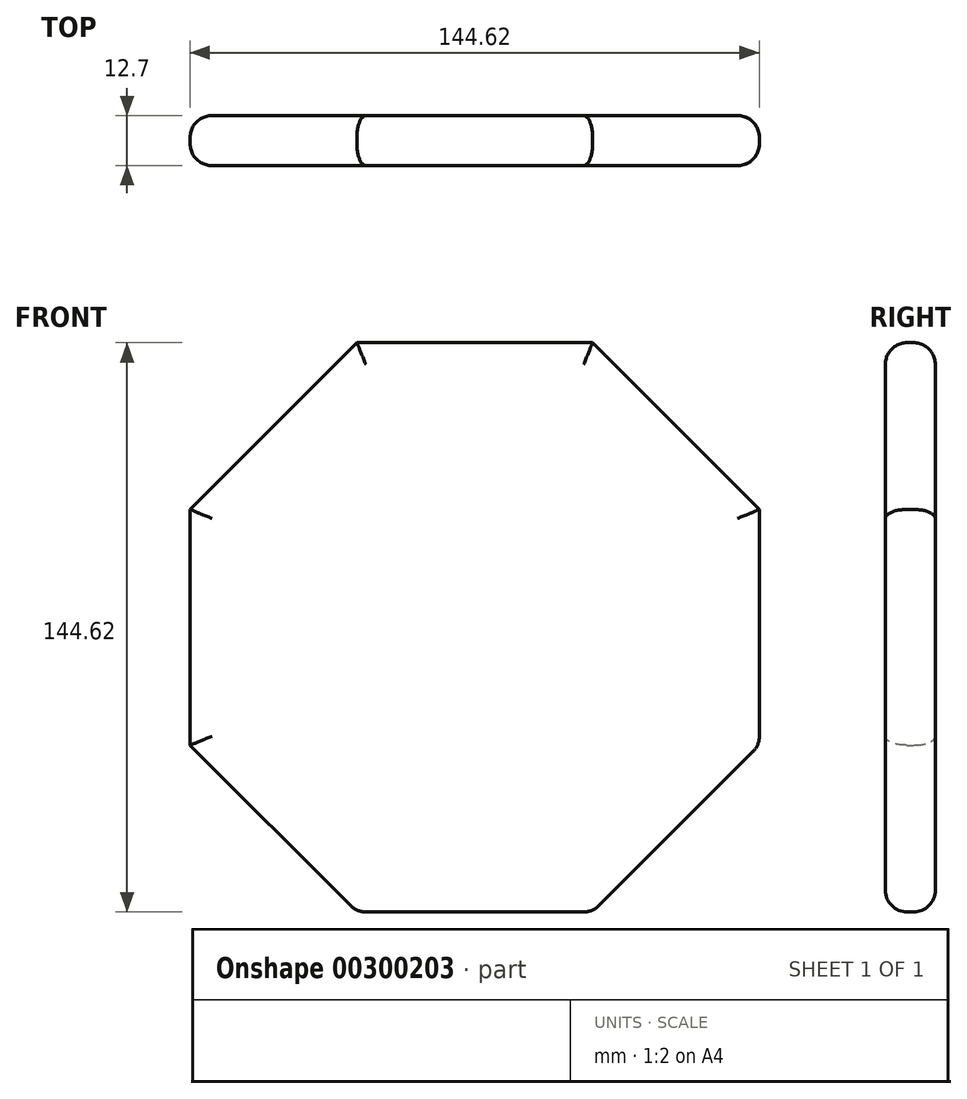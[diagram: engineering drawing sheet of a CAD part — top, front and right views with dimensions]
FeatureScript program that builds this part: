
annotation { "Feature Type Name" : "Feature", "Feature Type Description" : "" }
export const myFeature = defineFeature(function(context is Context, id is Id, definition is map)
    precondition{}
    {
        {
            var Q0;
            Q0=qCreatedBy(makeId("Front.planeOp"),FACE);
            var sketch = newSketch(context, id + "F0", { "sketchPlane" : qUnion([Q0])});
            skCircle(sketch, "E0.cCircle", {"center": v(0, 0) * mm, "radius": 72.31 * mm, "construction": true});
            skLineSegment(sketch, "E0.0", {"start": v(-72.31, -29.95) * mm, "end": v(-72.31, 29.95) * mm});
            skLineSegment(sketch, "E0.1", {"start": v(-72.31, 29.95) * mm, "end": v(-29.95, 72.31) * mm});
            skLineSegment(sketch, "E0.2", {"start": v(-29.95, 72.31) * mm, "end": v(29.95, 72.31) * mm});
            skLineSegment(sketch, "E0.3", {"start": v(29.95, 72.31) * mm, "end": v(72.31, 29.95) * mm});
            skLineSegment(sketch, "E0.4", {"start": v(72.31, 29.95) * mm, "end": v(72.31, -29.95) * mm});
            skLineSegment(sketch, "E0.5", {"start": v(72.31, -29.95) * mm, "end": v(29.95, -72.31) * mm});
            skLineSegment(sketch, "E0.6", {"start": v(29.95, -72.31) * mm, "end": v(-29.95, -72.31) * mm});
            skLineSegment(sketch, "E0.7", {"start": v(-29.95, -72.31) * mm, "end": v(-72.31, -29.95) * mm});
            skPoint(sketch, "E0.0.midPoint", {"position": v(-72.31, 0) * mm});
            skSolve(sketch);
        }
        {
            var Q0;
            Q0 = qSketchRegion(id + "F0", true);
            extrude(context, id + "F1", {"entities" : qUnion([Q0]), "depth" : 12.7 * mm});
        }
        {
            var Q0;
            Q0=makeQuery(id+"F1.opExtrude","CAP_EDGE",EDGE,{"disambiguationData":[OSD([sQuery(id+"F0.wireOp",EDGE,"E0.3")])],"isStart":false});
            var Q1;
            Q1=makeQuery(id+"F1.opExtrude","CAP_EDGE",EDGE,{"disambiguationData":[OSD([sQuery(id+"F0.wireOp",EDGE,"E0.2")])],"isStart":false});
            var Q2;
            Q2=makeQuery(id+"F1.opExtrude","CAP_EDGE",EDGE,{"disambiguationData":[OSD([sQuery(id+"F0.wireOp",EDGE,"E0.4")])],"isStart":false});
            var Q3;
            Q3=makeQuery(id+"F1.opExtrude","CAP_EDGE",EDGE,{"disambiguationData":[OSD([sQuery(id+"F0.wireOp",EDGE,"E0.4")])],"isStart":true});
            var Q4;
            Q4=makeQuery(id+"F1.opExtrude","CAP_EDGE",EDGE,{"disambiguationData":[OSD([sQuery(id+"F0.wireOp",EDGE,"E0.3")])],"isStart":true});
            var Q5;
            Q5=makeQuery(id+"F1.opExtrude","CAP_EDGE",EDGE,{"disambiguationData":[OSD([sQuery(id+"F0.wireOp",EDGE,"E0.1")])],"isStart":false});
            var Q6;
            Q6=makeQuery(id+"F1.opExtrude","CAP_EDGE",EDGE,{"disambiguationData":[OSD([sQuery(id+"F0.wireOp",EDGE,"E0.0")])],"isStart":false});
            var Q7;
            Q7=makeQuery(id+"F1.opExtrude","CAP_EDGE",EDGE,{"disambiguationData":[OSD([sQuery(id+"F0.wireOp",EDGE,"E0.0")])],"isStart":true});
            var Q8;
            Q8=makeQuery(id+"F1.opExtrude","CAP_EDGE",EDGE,{"disambiguationData":[OSD([sQuery(id+"F0.wireOp",EDGE,"E0.2")])],"isStart":true});
            var Q9;
            Q9=makeQuery(id+"F1.opExtrude","CAP_EDGE",EDGE,{"disambiguationData":[OSD([sQuery(id+"F0.wireOp",EDGE,"E0.1")])],"isStart":true});
            var Q10;
            Q10=makeQuery(id+"F1.opExtrude","CAP_EDGE",EDGE,{"disambiguationData":[OSD([sQuery(id+"F0.wireOp",EDGE,"E0.7")])],"isStart":false});
            var Q11;
            Q11=makeQuery(id+"F1.opExtrude","CAP_EDGE",EDGE,{"disambiguationData":[OSD([sQuery(id+"F0.wireOp",EDGE,"E0.7")])],"isStart":true});
            var Q12;
            Q12=makeQuery(id+"F1.opExtrude","SWEPT_FACE",FACE,{"disambiguationData":[OSD([sQuery(id+"F0.wireOp",EDGE,"E0.6")])]});
            var Q13;
            Q13=makeQuery(id+"F1.opExtrude","SWEPT_FACE",FACE,{"disambiguationData":[OSD([sQuery(id+"F0.wireOp",EDGE,"E0.5")])]});
            fillet(context, id + "F2", {"entities" : qUnion([Q0, Q1, Q2, Q3, Q4, Q5, Q6, Q7, Q8, Q9, Q10, Q11, Q12, Q13]), "radius" : 5.52 * mm, "tangentPropagation" : true, "allowEdgeOverflow" : false});
        }
    });
